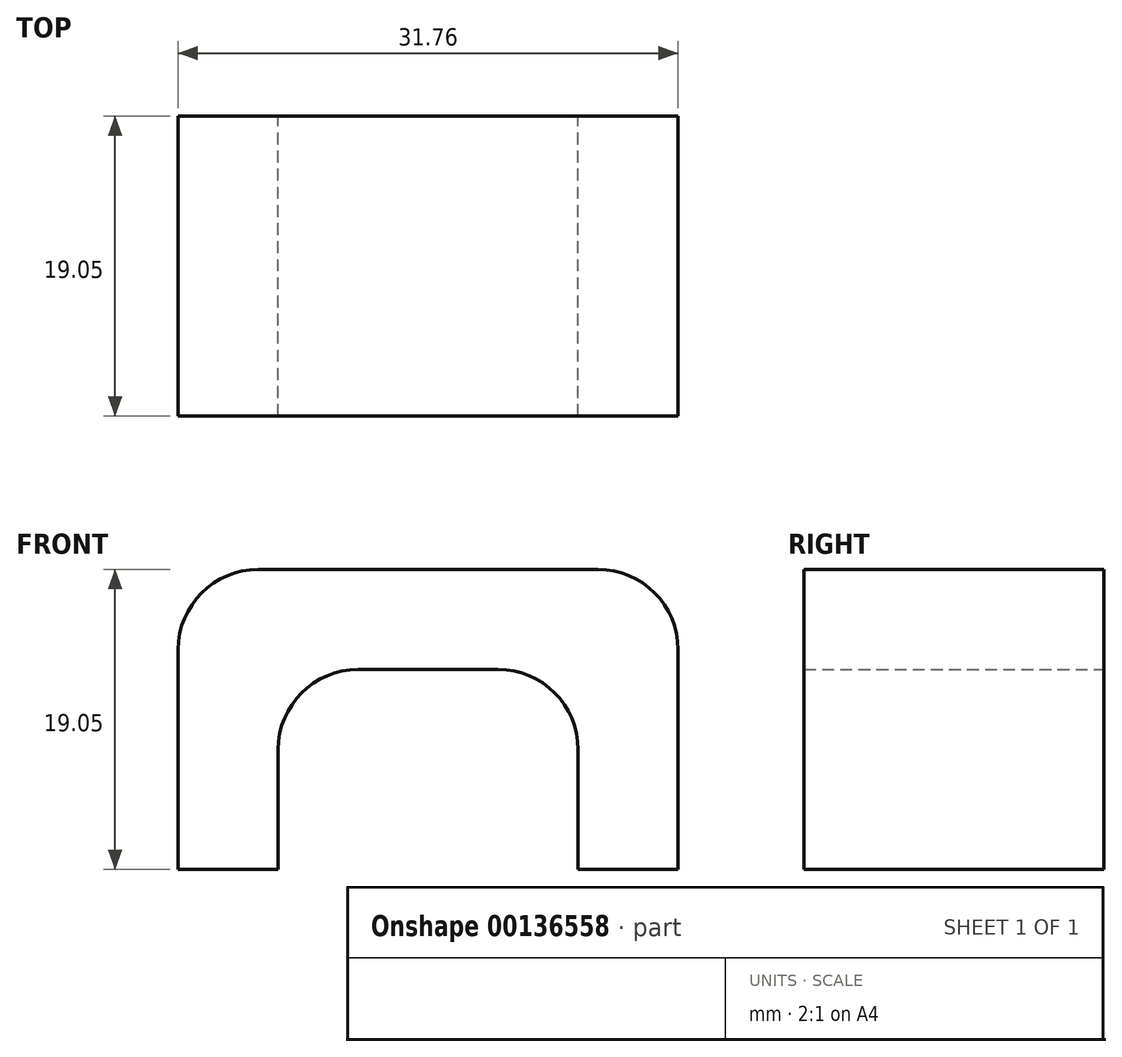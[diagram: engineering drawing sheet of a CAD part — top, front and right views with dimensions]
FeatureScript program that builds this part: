
annotation { "Feature Type Name" : "Feature", "Feature Type Description" : "" }
export const myFeature = defineFeature(function(context is Context, id is Id, definition is map)
    precondition{}
    {
        {
            var Q0;
            Q0=qCreatedBy(makeId("Front.planeOp"),FACE);
            var sketch = newSketch(context, id + "F0", { "sketchPlane" : qUnion([Q0])});
            skLineSegment(sketch, "E0", {"start": v(0, 0) * mm, "end": v(-15.87, 0) * mm});
            skLineSegment(sketch, "E1", {"start": v(-15.87, 0) * mm, "end": v(-15.87, -19.05) * mm});
            skLineSegment(sketch, "E2", {"start": v(-15.87, -19.05) * mm, "end": v(-9.52, -19.05) * mm});
            skLineSegment(sketch, "E3", {"start": v(-9.52, -19.05) * mm, "end": v(-9.52, -6.35) * mm});
            skLineSegment(sketch, "E4", {"start": v(-9.52, -6.35) * mm, "end": v(0, -6.35) * mm});
            skLineSegment(sketch, "E5", {"start": v(0, -6.35) * mm, "end": v(0, 0) * mm, "construction": true});
            skLineSegment(sketch, "E6.MirrorCS", {"start": v(15.88, 0) * mm, "end": v(15.88, -19.05) * mm});
            skLineSegment(sketch, "E7.MirrorCS", {"start": v(15.87, -19.05) * mm, "end": v(9.52, -19.05) * mm});
            skLineSegment(sketch, "E8.MirrorCS", {"start": v(9.52, -19.05) * mm, "end": v(9.52, -6.35) * mm});
            skLineSegment(sketch, "E9.MirrorCS", {"start": v(0, 0) * mm, "end": v(15.87, 0) * mm});
            skLineSegment(sketch, "E10.MirrorCS", {"start": v(9.52, -6.35) * mm, "end": v(0, -6.35) * mm});
            skSolve(sketch);
        }
        {
            var Q0;
            Q0 = qSketchRegion(id + "F0", true);
            extrude(context, id + "F1", {"entities" : qUnion([Q0]), "depth" : 19.05 * mm});
        }
        {
            var Q0;
            Q0=makeQuery(id+"F1.opExtrude","SWEPT_EDGE",EDGE,{"disambiguationData":[OSD([sQuery(id+"F0.wireOp",EDGE,"E0"),sQuery(id+"F0.wireOp",EDGE,"E1")])]});
            var Q1;
            Q1=makeQuery(id+"F1.opExtrude","SWEPT_EDGE",EDGE,{"disambiguationData":[OSD([sQuery(id+"F0.wireOp",EDGE,"E3"),sQuery(id+"F0.wireOp",EDGE,"E4")])]});
            var Q2;
            Q2=makeQuery(id+"F1.opExtrude","SWEPT_EDGE",EDGE,{"disambiguationData":[OSD([sQuery(id+"F0.wireOp",EDGE,"E8.MirrorCS"),sQuery(id+"F0.wireOp",EDGE,"E10.MirrorCS")])]});
            var Q3;
            Q3=makeQuery(id+"F1.opExtrude","SWEPT_EDGE",EDGE,{"disambiguationData":[OSD([sQuery(id+"F0.wireOp",EDGE,"E6.MirrorCS"),sQuery(id+"F0.wireOp",EDGE,"E9.MirrorCS")])]});
            fillet(context, id + "F2", {"entities" : qUnion([Q0, Q1, Q2, Q3]), "radius" : 5.08 * mm, "tangentPropagation" : true, "allowEdgeOverflow" : false});
        }
    });
